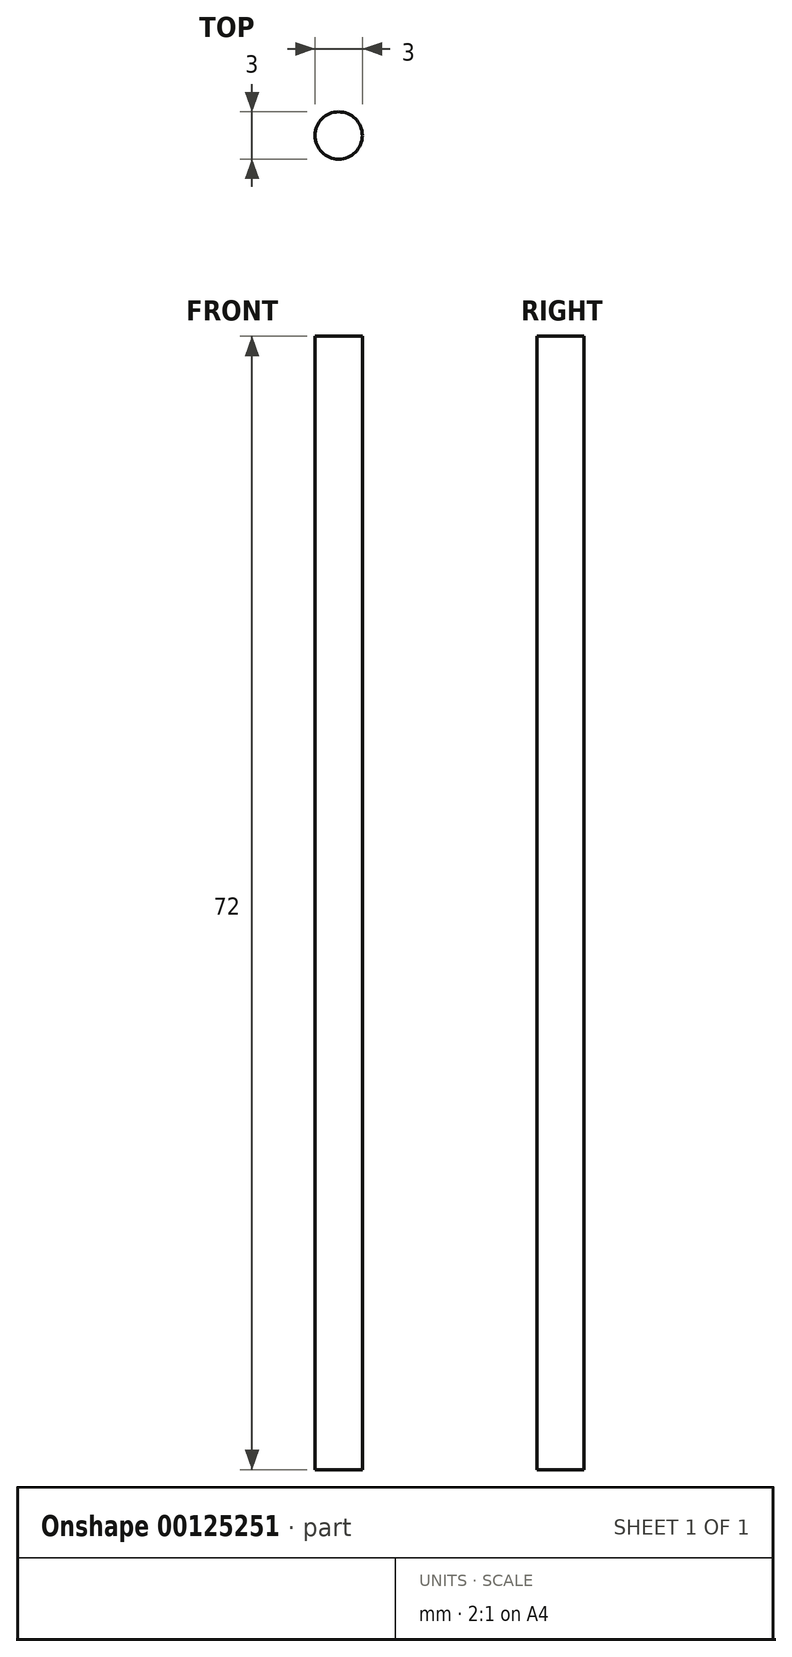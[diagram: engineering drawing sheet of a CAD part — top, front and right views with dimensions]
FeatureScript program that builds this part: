
annotation { "Feature Type Name" : "Feature", "Feature Type Description" : "" }
export const myFeature = defineFeature(function(context is Context, id is Id, definition is map)
    precondition{}
    {
        {
            assignVariable(context, id + "F0", {"name" : "a", "anyValue" : 72});
        }
        {
            var Q0;
            Q0=qCreatedBy(makeId("Top.planeOp"),FACE);
            var sketch = newSketch(context, id + "F1", { "sketchPlane" : qUnion([Q0])});
            skCircle(sketch, "E0", {"center": v(0, 0) * mm, "radius": 1.5 * mm});
            skSolve(sketch);
        }
        {
            var Q0;
            Q0=makeQuery(id+"F1.imprint","IMPRINT",FACE,{"disambiguationData":[TD([[makeQuery(id+"F1.imprint","IMPRINT",EDGE,{"derivedFrom":sQuery(id+"F1.wireOp",EDGE,"E0")}),1.0]])]});
            extrude(context, id + "F2", {"entities" : qUnion([Q0]), "depth" : getVariable(context, 'a') * mm});
        }
    });
